# Revit family: Haworth_Auckland_SwivelChair
name_source: partatom
category: Furniture
revit_build: Autodesk Revit 2018 (Build: 20170223_1515(x64)
units: mm (PartAtom-declared; Revit-internal decimal feet)

## family parameters
Always vertical = Yes
Cut with Voids When Loaded = No
OmniClass Number = 23.40.20.00
OmniClass Title = General Furniture and Specialties
Room Calculation Point = No
Shared = No
Work Plane-Based = No

## types (2) — shared parameters
Assembly Code = E2020200
Manufacturer = Haworth
Revision = 4
Size = Verify Final Dim. w/ Haworth
Standard Depth = 34 inches
Standard Width = 31 inches
URL = http://www.haworth.com
URL - Product = http://www.haworth.com
Warranty = http://www.haworth.com

## per-type parameters (varying)
| type | Description | Head Rest | Model | Standard Height |
| HCCS-AUC3 - With Headrest | Haworth Auckland Swivel Chair - With Headrest | Yes | HCCS-AUC3 | 39 inches |
| HCCS-AUC2 - Without Headrest | Haworth Auckland Swivel Chair - Without Headrest | No | HCCS-AUC2 | 28 inches |

## geometry (parser evidence)
native form markers: Sweep x2
no freeform markers — native parametric forms only
